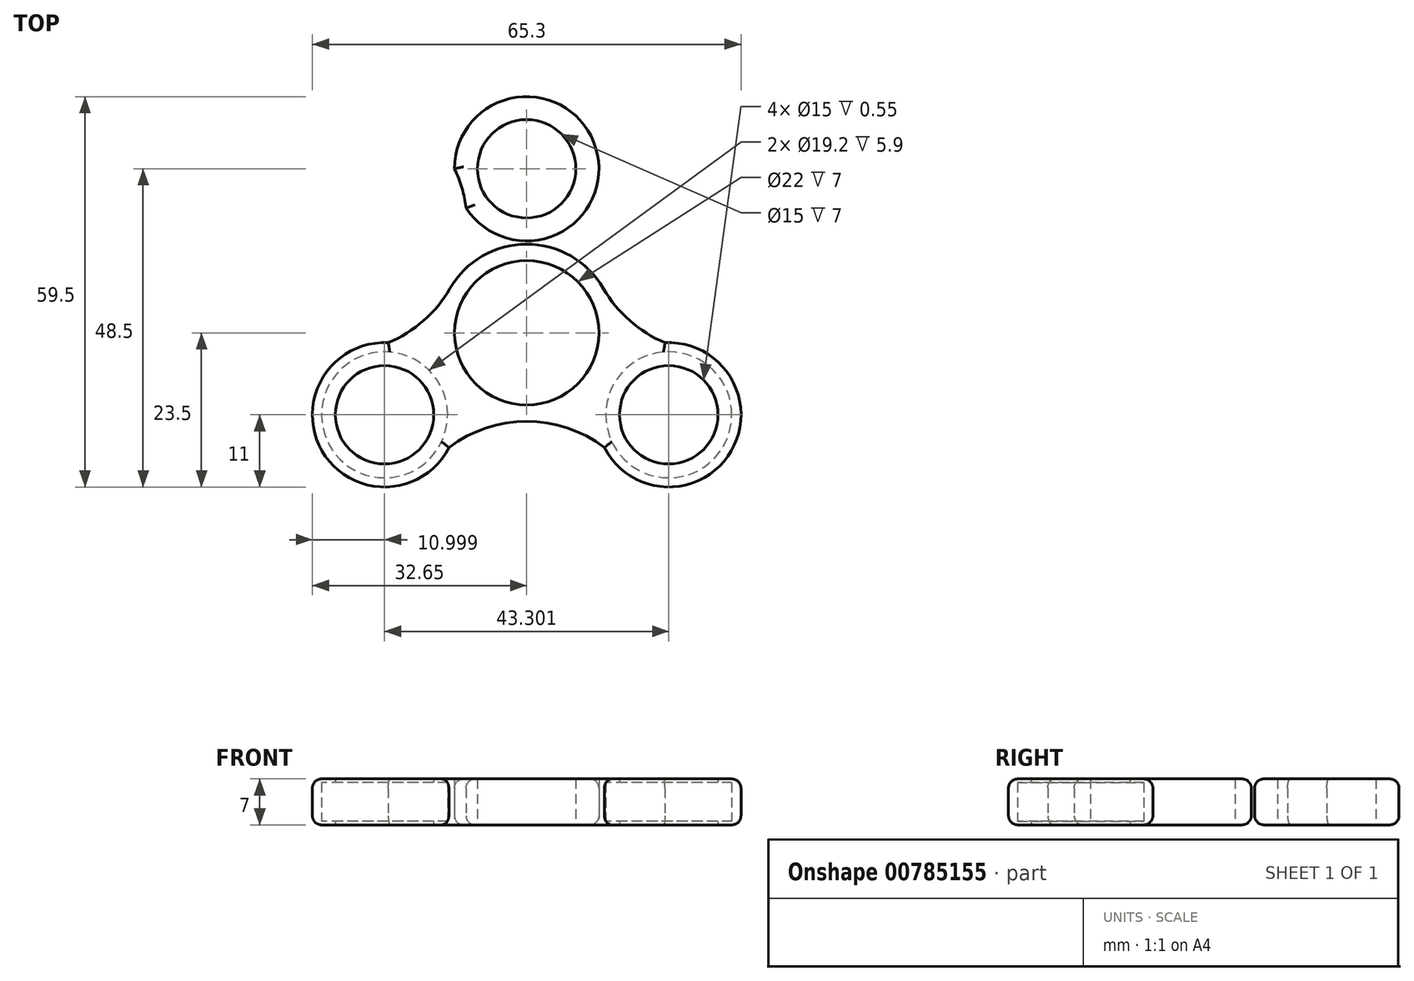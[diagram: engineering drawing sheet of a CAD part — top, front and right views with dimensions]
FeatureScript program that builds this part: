
annotation { "Feature Type Name" : "Feature", "Feature Type Description" : "" }
export const myFeature = defineFeature(function(context is Context, id is Id, definition is map)
    precondition{}
    {
        {
            var Q0;
            Q0=qCreatedBy(makeId("Top.planeOp"),FACE);
            var sketch = newSketch(context, id + "F0", { "sketchPlane" : qUnion([Q0])});
            skLineSegment(sketch, "E0", {"start": v(0, 0) * mm, "end": v(0, 25) * mm, "construction": true});
            skLineSegment(sketch, "E1", {"start": v(0, 0) * mm, "end": v(-21.65, -12.5) * mm, "construction": true});
            skLineSegment(sketch, "E2", {"start": v(0, 0) * mm, "end": v(21.65, -12.5) * mm, "construction": true});
            skLineSegment(sketch, "E3", {"start": v(0, 25) * mm, "end": v(-21.65, -12.5) * mm, "construction": true});
            skLineSegment(sketch, "E4", {"start": v(-21.65, -12.5) * mm, "end": v(21.65, -12.5) * mm, "construction": true});
            skLineSegment(sketch, "E5", {"start": v(21.65, -12.5) * mm, "end": v(0, 25) * mm, "construction": true});
            skCircle(sketch, "E6", {"center": v(0, 0) * mm, "radius": 11 * mm});
            skCircle(sketch, "E7", {"center": v(0, 25) * mm, "radius": 9.55 * mm});
            skCircle(sketch, "E8", {"center": v(21.65, -12.5) * mm, "radius": 9.55 * mm});
            skCircle(sketch, "E9", {"center": v(-21.65, -12.5) * mm, "radius": 9.55 * mm});
            skCircle(sketch, "E10", {"center": v(0, 25) * mm, "radius": 11 * mm});
            skCircle(sketch, "E11", {"center": v(21.65, -12.5) * mm, "radius": 11 * mm});
            skCircle(sketch, "E12", {"center": v(-21.65, -12.5) * mm, "radius": 11 * mm});
            skCircle(sketch, "E13", {"center": v(0, 0) * mm, "radius": 13.5 * mm});
            skPoint(sketch, "E14", {"position": v(0, 13.5) * mm});
            skPoint(sketch, "E15", {"position": v(11.7, -6.75) * mm});
            skPoint(sketch, "E16", {"position": v(-11.7, -6.75) * mm});
            skPoint(sketch, "E17", {"position": v(-12.12, -7) * mm});
            skPoint(sketch, "E18", {"position": v(0, 14) * mm});
            skPoint(sketch, "E19", {"position": v(12.12, -7) * mm});
            skLineSegment(sketch, "E20", {"start": v(0, 13.5) * mm, "end": v(-11.7, -6.75) * mm, "construction": true});
            skLineSegment(sketch, "E21", {"start": v(11.7, -6.75) * mm, "end": v(-11.7, -6.75) * mm, "construction": true});
            skLineSegment(sketch, "E22", {"start": v(0, 13.5) * mm, "end": v(11.7, -6.75) * mm, "construction": true});
            skLineSegment(sketch, "E23", {"start": v(-5.85, 3.37) * mm, "end": v(-11.7, 6.75) * mm, "construction": true});
            skLineSegment(sketch, "E24", {"start": v(5.85, 3.37) * mm, "end": v(11.7, 6.75) * mm, "construction": true});
            skLineSegment(sketch, "E25", {"start": v(0, -6.75) * mm, "end": v(0, -13.5) * mm, "construction": true});
            skLineSegment(sketch, "E26", {"start": v(0, 25) * mm, "end": v(-11, 25) * mm, "construction": true});
            skLineSegment(sketch, "E27", {"start": v(0, 25) * mm, "end": v(11, 25) * mm, "construction": true});
            skLineSegment(sketch, "E28", {"start": v(21.65, -12.5) * mm, "end": v(27.15, -2.97) * mm, "construction": true});
            skLineSegment(sketch, "E29", {"start": v(21.65, -12.5) * mm, "end": v(16.15, -22.03) * mm, "construction": true});
            skLineSegment(sketch, "E30", {"start": v(-21.65, -12.5) * mm, "end": v(-27.15, -2.97) * mm, "construction": true});
            skLineSegment(sketch, "E31", {"start": v(-21.65, -12.5) * mm, "end": v(-16.15, -22.03) * mm, "construction": true});
            skArc(sketch, "E32", {"start": v(11, 25) * mm, "mid": v(11.7, 6.75) * mm, "end": v(27.15, -2.97) * mm});
            skArc(sketch, "E33", {"start": v(-27.15, -2.97) * mm, "mid": v(-11.7, 6.75) * mm, "end": v(-11, 25) * mm});
            skArc(sketch, "E34", {"start": v(16.15, -22.03) * mm, "mid": v(0, -13.5) * mm, "end": v(-16.15, -22.03) * mm});
            skSolve(sketch);
        }
        {
            var Q0;
            Q0=makeQuery(id+"F0.imprint","IMPRINT",FACE,{"disambiguationData":[TD([[makeQuery(id+"F0.imprint","IMPRINT",EDGE,{"derivedFrom":sQuery(id+"F0.wireOp",EDGE,"E7")}),-1.0]])]});
            var Q1;
            {var subQ0=sQuery(id+"F0.wireOp",EDGE,"E32");var subQ1=sQuery(id+"F0.wireOp",EDGE,"E10");var subQ2=makeQuery(id+"F0.imprint","INTERSECT",VERTEX,{"disambiguationData":[OD(0.0)],"derivedFrom":[subQ1,subQ0]});Q1=makeQuery(id+"F0.imprint","IMPRINT",FACE,{"disambiguationData":[TD([[makeQuery(id+"F0.imprint","IMPRINT",EDGE,{"disambiguationData":[TD([[subQ2,1.0]])],"derivedFrom":subQ1}),1.0]])]});}
            var Q2;
            {var subQ0=sQuery(id+"F0.wireOp",EDGE,"E33");var subQ1=sQuery(id+"F0.wireOp",EDGE,"E10");var subQ2=makeQuery(id+"F0.imprint","INTERSECT",VERTEX,{"disambiguationData":[OD(0.0)],"derivedFrom":[subQ1,subQ0]});Q2=makeQuery(id+"F0.imprint","IMPRINT",FACE,{"disambiguationData":[TD([[makeQuery(id+"F0.imprint","IMPRINT",EDGE,{"disambiguationData":[TD([[subQ2,-1.0]])],"derivedFrom":subQ1}),1.0]])]});}
            var Q3;
            Q3=makeQuery(id+"F0.imprint","IMPRINT",FACE,{"disambiguationData":[TD([[makeQuery(id+"F0.imprint","IMPRINT",EDGE,{"derivedFrom":sQuery(id+"F0.wireOp",EDGE,"E7")}),1.0]])]});
            var Q4;
            {var subQ0=sQuery(id+"F0.wireOp",EDGE,"E33");var subQ1=sQuery(id+"F0.wireOp",EDGE,"E10");var subQ2=makeQuery(id+"F0.imprint","INTERSECT",VERTEX,{"disambiguationData":[OD(1.0)],"derivedFrom":[subQ1,subQ0]});Q4=makeQuery(id+"F0.imprint","IMPRINT",FACE,{"disambiguationData":[TD([[makeQuery(id+"F0.imprint","IMPRINT",EDGE,{"disambiguationData":[TD([[subQ2,-1.0]])],"derivedFrom":subQ1}),-1.0]])]});}
            var Q5;
            {var subQ0=sQuery(id+"F0.wireOp",EDGE,"E32");var subQ1=sQuery(id+"F0.wireOp",EDGE,"E11");var subQ2=makeQuery(id+"F0.imprint","INTERSECT",VERTEX,{"disambiguationData":[OD(0.0)],"derivedFrom":[subQ1,subQ0]});Q5=makeQuery(id+"F0.imprint","IMPRINT",FACE,{"disambiguationData":[TD([[makeQuery(id+"F0.imprint","IMPRINT",EDGE,{"disambiguationData":[TD([[subQ2,-1.0]])],"derivedFrom":subQ1}),1.0]])]});}
            var Q6;
            Q6=makeQuery(id+"F0.imprint","IMPRINT",FACE,{"disambiguationData":[TD([[makeQuery(id+"F0.imprint","IMPRINT",EDGE,{"derivedFrom":sQuery(id+"F0.wireOp",EDGE,"E8")}),-1.0]])]});
            var Q7;
            Q7=makeQuery(id+"F0.imprint","IMPRINT",FACE,{"disambiguationData":[TD([[makeQuery(id+"F0.imprint","IMPRINT",EDGE,{"derivedFrom":sQuery(id+"F0.wireOp",EDGE,"E8")}),1.0]])]});
            var Q8;
            {var subQ0=sQuery(id+"F0.wireOp",EDGE,"E34");var subQ1=sQuery(id+"F0.wireOp",EDGE,"E11");var subQ2=makeQuery(id+"F0.imprint","INTERSECT",VERTEX,{"disambiguationData":[OD(0.0)],"derivedFrom":[subQ1,subQ0]});Q8=makeQuery(id+"F0.imprint","IMPRINT",FACE,{"disambiguationData":[TD([[makeQuery(id+"F0.imprint","IMPRINT",EDGE,{"disambiguationData":[TD([[subQ2,1.0]])],"derivedFrom":subQ1}),1.0]])]});}
            var Q9;
            {var subQ0=sQuery(id+"F0.wireOp",EDGE,"E32");var subQ1=sQuery(id+"F0.wireOp",EDGE,"E11");var subQ2=makeQuery(id+"F0.imprint","INTERSECT",VERTEX,{"disambiguationData":[OD(1.0)],"derivedFrom":[subQ1,subQ0]});Q9=makeQuery(id+"F0.imprint","IMPRINT",FACE,{"disambiguationData":[TD([[makeQuery(id+"F0.imprint","IMPRINT",EDGE,{"disambiguationData":[TD([[subQ2,-1.0]])],"derivedFrom":subQ1}),-1.0]])]});}
            var Q10;
            Q10=makeQuery(id+"F0.imprint","IMPRINT",FACE,{"disambiguationData":[TD([[makeQuery(id+"F0.imprint","IMPRINT",EDGE,{"derivedFrom":sQuery(id+"F0.wireOp",EDGE,"E6")}),-1.0]])]});
            var Q11;
            {var subQ0=sQuery(id+"F0.wireOp",EDGE,"E33");var subQ1=sQuery(id+"F0.wireOp",EDGE,"E12");var subQ2=makeQuery(id+"F0.imprint","INTERSECT",VERTEX,{"disambiguationData":[OD(0.0)],"derivedFrom":[subQ1,subQ0]});Q11=makeQuery(id+"F0.imprint","IMPRINT",FACE,{"disambiguationData":[TD([[makeQuery(id+"F0.imprint","IMPRINT",EDGE,{"disambiguationData":[TD([[subQ2,1.0]])],"derivedFrom":subQ1}),1.0]])]});}
            var Q12;
            Q12=makeQuery(id+"F0.imprint","IMPRINT",FACE,{"disambiguationData":[TD([[makeQuery(id+"F0.imprint","IMPRINT",EDGE,{"derivedFrom":sQuery(id+"F0.wireOp",EDGE,"E9")}),-1.0]])]});
            var Q13;
            Q13=makeQuery(id+"F0.imprint","IMPRINT",FACE,{"disambiguationData":[TD([[makeQuery(id+"F0.imprint","IMPRINT",EDGE,{"derivedFrom":sQuery(id+"F0.wireOp",EDGE,"E9")}),1.0]])]});
            var Q14;
            {var subQ0=sQuery(id+"F0.wireOp",EDGE,"E34");var subQ1=sQuery(id+"F0.wireOp",EDGE,"E12");var subQ2=makeQuery(id+"F0.imprint","INTERSECT",VERTEX,{"disambiguationData":[OD(0.0)],"derivedFrom":[subQ1,subQ0]});Q14=makeQuery(id+"F0.imprint","IMPRINT",FACE,{"disambiguationData":[TD([[makeQuery(id+"F0.imprint","IMPRINT",EDGE,{"disambiguationData":[TD([[subQ2,-1.0]])],"derivedFrom":subQ1}),1.0]])]});}
            var Q15;
            {var subQ0=sQuery(id+"F0.wireOp",EDGE,"E33");var subQ1=sQuery(id+"F0.wireOp",EDGE,"E12");var subQ2=makeQuery(id+"F0.imprint","INTERSECT",VERTEX,{"disambiguationData":[OD(1.0)],"derivedFrom":[subQ1,subQ0]});Q15=makeQuery(id+"F0.imprint","IMPRINT",FACE,{"disambiguationData":[TD([[makeQuery(id+"F0.imprint","IMPRINT",EDGE,{"disambiguationData":[TD([[subQ2,1.0]])],"derivedFrom":subQ1}),-1.0]])]});}
            extrude(context, id + "F1", {"entities" : qUnion([Q0, Q1, Q2, Q3, Q4, Q5, Q6, Q7, Q8, Q9, Q10, Q11, Q12, Q13, Q14, Q15]), "depth" : 7 * mm, "offsetDistance" : 25 * mm});
        }
        {
            var Q0;
            Q0=makeQuery(id+"F1.opExtrude","CAP_FACE",FACE,{"disambiguationData":[OSD([sQuery(id+"F0.wireOp",EDGE,"E6"),sQuery(id+"F0.wireOp",EDGE,"E10"),sQuery(id+"F0.wireOp",EDGE,"E11"),sQuery(id+"F0.wireOp",EDGE,"E12"),sQuery(id+"F0.wireOp",EDGE,"E32"),sQuery(id+"F0.wireOp",EDGE,"E33"),sQuery(id+"F0.wireOp",EDGE,"E34")])],"isStart":false});
            var sketch = newSketch(context, id + "F2", { "sketchPlane" : qUnion([Q0])});
            skCircle(sketch, "E35", {"center": v(21.65, -12.5) * mm, "radius": 9.6 * mm});
            skCircle(sketch, "E36", {"center": v(-21.65, -12.5) * mm, "radius": 9.6 * mm});
            skCircle(sketch, "E37", {"center": v(0, 25) * mm, "radius": 9.6 * mm});
            skSolve(sketch);
        }
        {
            var Q0;
            Q0=makeQuery(id+"F2.imprint","IMPRINT",FACE,{"disambiguationData":[TD([[makeQuery(id+"F2.imprint","IMPRINT",EDGE,{"derivedFrom":sQuery(id+"F2.wireOp",EDGE,"E35")}),1.0]])]});
            var Q1;
            Q1=makeQuery(id+"F2.imprint","IMPRINT",FACE,{"disambiguationData":[TD([[makeQuery(id+"F2.imprint","IMPRINT",EDGE,{"derivedFrom":sQuery(id+"F2.wireOp",EDGE,"E36")}),1.0]])]});
            var Q2;
            Q2=makeQuery(id+"F2.imprint","IMPRINT",FACE,{"disambiguationData":[TD([[makeQuery(id+"F2.imprint","IMPRINT",EDGE,{"derivedFrom":sQuery(id+"F2.wireOp",EDGE,"E37")}),1.0]])]});
            extrude(context, id + "F3", {"entities" : qUnion([Q0, Q1, Q2]), "depth" : 5.9 * mm, "offsetDistance" : 25 * mm});
        }
        {
            var Q0;
            Q0=makeQuery(id+"F3.opExtrude","SWEPT_BODY",BODY,{"disambiguationData":[OSD([sQuery(id+"F2.wireOp",EDGE,"E35")])]});
            var Q1;
            Q1=makeQuery(id+"F3.opExtrude","SWEPT_BODY",BODY,{"disambiguationData":[OSD([sQuery(id+"F2.wireOp",EDGE,"E36")])]});
            var Q2;
            Q2=makeQuery(id+"F3.opExtrude","SWEPT_BODY",BODY,{"disambiguationData":[OSD([sQuery(id+"F2.wireOp",EDGE,"E37")])]});
            transform(context, id + "F4", {"entities" : qUnion([Q0, Q1, Q2]), "transformType" : TransformType.TRANSLATION_3D, "dx" : 0 * mm, "dy" : 0 * mm, "dz" : -6.45 * mm, "makeCopy" : false});
        }
        {
            var Q0;
            Q0=makeQuery(id+"F1.opExtrude","CAP_EDGE",EDGE,{"disambiguationData":[OSD([sQuery(id+"F0.wireOp",EDGE,"E11")])],"isStart":false});
            var Q1;
            Q1=makeQuery(id+"F1.opExtrude","CAP_EDGE",EDGE,{"disambiguationData":[OSD([sQuery(id+"F0.wireOp",EDGE,"E32")])],"isStart":false});
            var Q2;
            Q2=makeQuery(id+"F1.opExtrude","CAP_EDGE",EDGE,{"disambiguationData":[OSD([sQuery(id+"F0.wireOp",EDGE,"E34")])],"isStart":false});
            var Q3;
            Q3=makeQuery(id+"F1.opExtrude","CAP_EDGE",EDGE,{"disambiguationData":[OSD([sQuery(id+"F0.wireOp",EDGE,"E12")])],"isStart":false});
            var Q4;
            Q4=makeQuery(id+"F1.opExtrude","CAP_EDGE",EDGE,{"disambiguationData":[OSD([sQuery(id+"F0.wireOp",EDGE,"E33")])],"isStart":false});
            var Q5;
            Q5=makeQuery(id+"F1.opExtrude","CAP_EDGE",EDGE,{"disambiguationData":[OSD([sQuery(id+"F0.wireOp",EDGE,"E10")])],"isStart":false});
            var Q6;
            Q6=makeQuery(id+"F1.opExtrude","CAP_EDGE",EDGE,{"disambiguationData":[OSD([sQuery(id+"F0.wireOp",EDGE,"E32")])],"isStart":true});
            var Q7;
            Q7=makeQuery(id+"F1.opExtrude","CAP_EDGE",EDGE,{"disambiguationData":[OSD([sQuery(id+"F0.wireOp",EDGE,"E11")])],"isStart":true});
            var Q8;
            Q8=makeQuery(id+"F1.opExtrude","CAP_EDGE",EDGE,{"disambiguationData":[OSD([sQuery(id+"F0.wireOp",EDGE,"E12")])],"isStart":true});
            var Q9;
            Q9=makeQuery(id+"F1.opExtrude","CAP_EDGE",EDGE,{"disambiguationData":[OSD([sQuery(id+"F0.wireOp",EDGE,"E34")])],"isStart":true});
            var Q10;
            Q10=makeQuery(id+"F1.opExtrude","CAP_EDGE",EDGE,{"disambiguationData":[OSD([sQuery(id+"F0.wireOp",EDGE,"E33")])],"isStart":true});
            var Q11;
            Q11=makeQuery(id+"F1.opExtrude","CAP_EDGE",EDGE,{"disambiguationData":[OSD([sQuery(id+"F0.wireOp",EDGE,"E10")])],"isStart":true});
            fillet(context, id + "F5", {"entities" : qUnion([Q0, Q1, Q2, Q3, Q4, Q5, Q6, Q7, Q8, Q9, Q10, Q11]), "radius" : 1.4 * mm, "tangentPropagation" : true, "allowEdgeOverflow" : false});
        }
        {
            var Q0;
            Q0=makeQuery(id+"F1.opExtrude","CAP_FACE",FACE,{"disambiguationData":[OSD([sQuery(id+"F0.wireOp",EDGE,"E6"),sQuery(id+"F0.wireOp",EDGE,"E10"),sQuery(id+"F0.wireOp",EDGE,"E11"),sQuery(id+"F0.wireOp",EDGE,"E12"),sQuery(id+"F0.wireOp",EDGE,"E32"),sQuery(id+"F0.wireOp",EDGE,"E33"),sQuery(id+"F0.wireOp",EDGE,"E34")])],"isStart":true});
            var sketch = newSketch(context, id + "F6", { "sketchPlane" : qUnion([Q0])});
            skCircle(sketch, "E38", {"center": v(21.65, 12.5) * mm, "radius": 7.5 * mm});
            skCircle(sketch, "E39", {"center": v(-21.65, 12.5) * mm, "radius": 7.5 * mm});
            skCircle(sketch, "E40", {"center": v(0, -25) * mm, "radius": 7.5 * mm});
            skSolve(sketch);
        }
        {
            var Q0;
            Q0=makeQuery(id+"F6.imprint","IMPRINT",FACE,{"disambiguationData":[TD([[makeQuery(id+"F6.imprint","IMPRINT",EDGE,{"derivedFrom":sQuery(id+"F6.wireOp",EDGE,"E38")}),1.0]])]});
            var Q1;
            Q1=makeQuery(id+"F6.imprint","IMPRINT",FACE,{"disambiguationData":[TD([[makeQuery(id+"F6.imprint","IMPRINT",EDGE,{"derivedFrom":sQuery(id+"F6.wireOp",EDGE,"E40")}),1.0]])]});
            var Q2;
            Q2=makeQuery(id+"F6.imprint","IMPRINT",FACE,{"disambiguationData":[TD([[makeQuery(id+"F6.imprint","IMPRINT",EDGE,{"derivedFrom":sQuery(id+"F6.wireOp",EDGE,"E39")}),1.0]])]});
            extrude(context, id + "F7", {"entities" : qUnion([Q0, Q1, Q2]), "operationType" : NewBodyOperationType.REMOVE, "oppositeDirection" : true, "depth" : 25 * mm, "offsetDistance" : 25 * mm});
        }
        {
            var Q0;
            Q0=makeQuery(id+"F3.opExtrude","SWEPT_BODY",BODY,{"disambiguationData":[OSD([sQuery(id+"F2.wireOp",EDGE,"E35")])]});
            var Q1;
            Q1=makeQuery(id+"F3.opExtrude","SWEPT_BODY",BODY,{"disambiguationData":[OSD([sQuery(id+"F2.wireOp",EDGE,"E36")])]});
            var Q2;
            Q2=makeQuery(id+"F3.opExtrude","SWEPT_BODY",BODY,{"disambiguationData":[OSD([sQuery(id+"F2.wireOp",EDGE,"E37")])]});
            var Q3;
            Q3=makeQuery(id+"F1.opExtrude","SWEPT_BODY",BODY,{"disambiguationData":[OSD([sQuery(id+"F0.wireOp",EDGE,"E6"),sQuery(id+"F0.wireOp",EDGE,"E10"),sQuery(id+"F0.wireOp",EDGE,"E11"),sQuery(id+"F0.wireOp",EDGE,"E12"),sQuery(id+"F0.wireOp",EDGE,"E32"),sQuery(id+"F0.wireOp",EDGE,"E33"),sQuery(id+"F0.wireOp",EDGE,"E34")])]});
            booleanBodies(context, id + "F8", {"operationType" : BooleanOperationType.SUBTRACTION, "tools" : qUnion([Q0, Q1, Q2]), "targets" : qUnion([Q3])});
        }
    });
